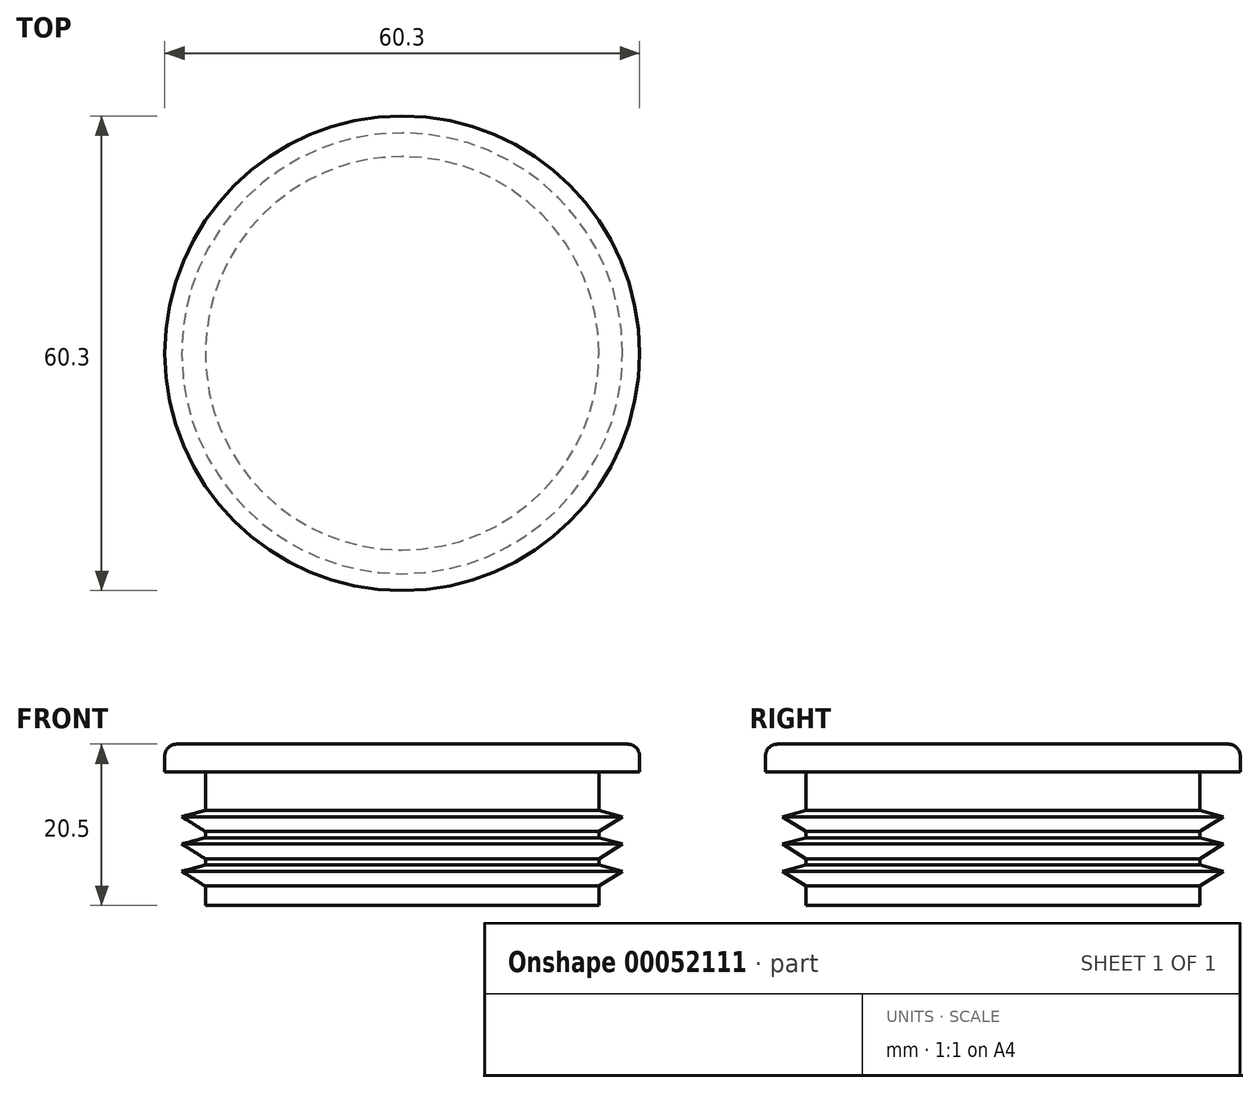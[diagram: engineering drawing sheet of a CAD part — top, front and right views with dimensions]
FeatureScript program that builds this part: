
annotation { "Feature Type Name" : "Feature", "Feature Type Description" : "" }
export const myFeature = defineFeature(function(context is Context, id is Id, definition is map)
    precondition{}
    {
        {
            var Q0;
            Q0=qCreatedBy(makeId("Right.planeOp"),FACE);
            var sketch = newSketch(context, id + "F0", { "sketchPlane" : qUnion([Q0])});
            skLineSegment(sketch, "E0", {"start": v(0, 20.5) * mm, "end": v(-28.65, 20.5) * mm});
            skLineSegment(sketch, "E1", {"start": v(-30.15, 19) * mm, "end": v(-30.15, 17) * mm});
            skLineSegment(sketch, "E2", {"start": v(-30.15, 17) * mm, "end": v(-25, 17) * mm});
            skLineSegment(sketch, "E3", {"start": v(-25, 17) * mm, "end": v(-25, 0) * mm});
            skLineSegment(sketch, "E4", {"start": v(-25, 0) * mm, "end": v(0, 0) * mm});
            skLineSegment(sketch, "E5", {"start": v(0, 0) * mm, "end": v(0, 20.5) * mm});
            skPoint(sketch, "E6.visualSharp", {"position": v(-30.15, 20.5) * mm});
            skArc(sketch, "E6.filletArc", {"start": v(-28.65, 20.5) * mm, "mid": v(-29.71, 20.06) * mm, "end": v(-30.15, 19) * mm});
            skLineSegment(sketch, "E7", {"start": v(-25, 11.28) * mm, "end": v(-28, 11.28) * mm});
            skLineSegment(sketch, "E8", {"start": v(-28, 11.28) * mm, "end": v(-25, 9.41) * mm});
            skLineSegment(sketch, "E9", {"start": v(-25, 9.41) * mm, "end": v(-25, 7.8) * mm});
            skLineSegment(sketch, "E10", {"start": v(-25, 7.8) * mm, "end": v(-28, 7.8) * mm});
            skLineSegment(sketch, "E11", {"start": v(-28, 7.8) * mm, "end": v(-25, 5.94) * mm});
            skLineSegment(sketch, "E12", {"start": v(-25, 5.94) * mm, "end": v(-25, 4.34) * mm});
            skLineSegment(sketch, "E13", {"start": v(-25, 4.34) * mm, "end": v(-28, 4.34) * mm});
            skLineSegment(sketch, "E14", {"start": v(-28, 4.34) * mm, "end": v(-25, 2.47) * mm});
            skLineSegment(sketch, "E15", {"start": v(-28, 11.28) * mm, "end": v(-25, 12.08) * mm});
            skLineSegment(sketch, "E16", {"start": v(-28, 7.8) * mm, "end": v(-25, 8.61) * mm});
            skLineSegment(sketch, "E17", {"start": v(-28, 4.34) * mm, "end": v(-25, 5.14) * mm});
            skSolve(sketch);
        }
        {
            var Q0;
            {var subQ0=sQuery(id+"F0.wireOp",EDGE,"E10");var subQ6=makeQuery(id+"F0.imprint","IMPRINT",EDGE,{"derivedFrom":subQ0});var subQ7=sQuery(id+"F0.wireOp",EDGE,"E13");var subQ12=makeQuery(id+"F0.imprint","IMPRINT",EDGE,{"derivedFrom":subQ7});var subQ13=sQuery(id+"F0.wireOp",EDGE,"E7");var subQ18=makeQuery(id+"F0.imprint","IMPRINT",EDGE,{"derivedFrom":subQ13});Q0=qUnion([makeQuery(id+"F0.imprint","IMPRINT",FACE,{"disambiguationData":[TD([[subQ18,-1.0]])]}),makeQuery(id+"F0.imprint","IMPRINT",FACE,{"disambiguationData":[TD([[makeQuery(id+"F0.imprint","IMPRINT",EDGE,{"derivedFrom":sQuery(id+"F0.wireOp",EDGE,"E0")}),1.0]])]}),makeQuery(id+"F0.imprint","IMPRINT",FACE,{"disambiguationData":[TD([[subQ12,1.0]])]}),makeQuery(id+"F0.imprint","IMPRINT",FACE,{"disambiguationData":[TD([[subQ6,-1.0]])]}),makeQuery(id+"F0.imprint","IMPRINT",FACE,{"disambiguationData":[TD([[subQ18,1.0]])]}),makeQuery(id+"F0.imprint","IMPRINT",FACE,{"disambiguationData":[TD([[subQ12,-1.0]])]}),makeQuery(id+"F0.imprint","IMPRINT",FACE,{"disambiguationData":[TD([[subQ6,1.0]])]})]);}
            var Q1;
            Q1=sQuery(id+"F0.wireOp",EDGE,"E5");
            revolve(context, id + "F1", {"entities" : qUnion([Q0]), "axis" : qUnion([Q1]), "revolveType" : RevolveType.FULL});
        }
    });
